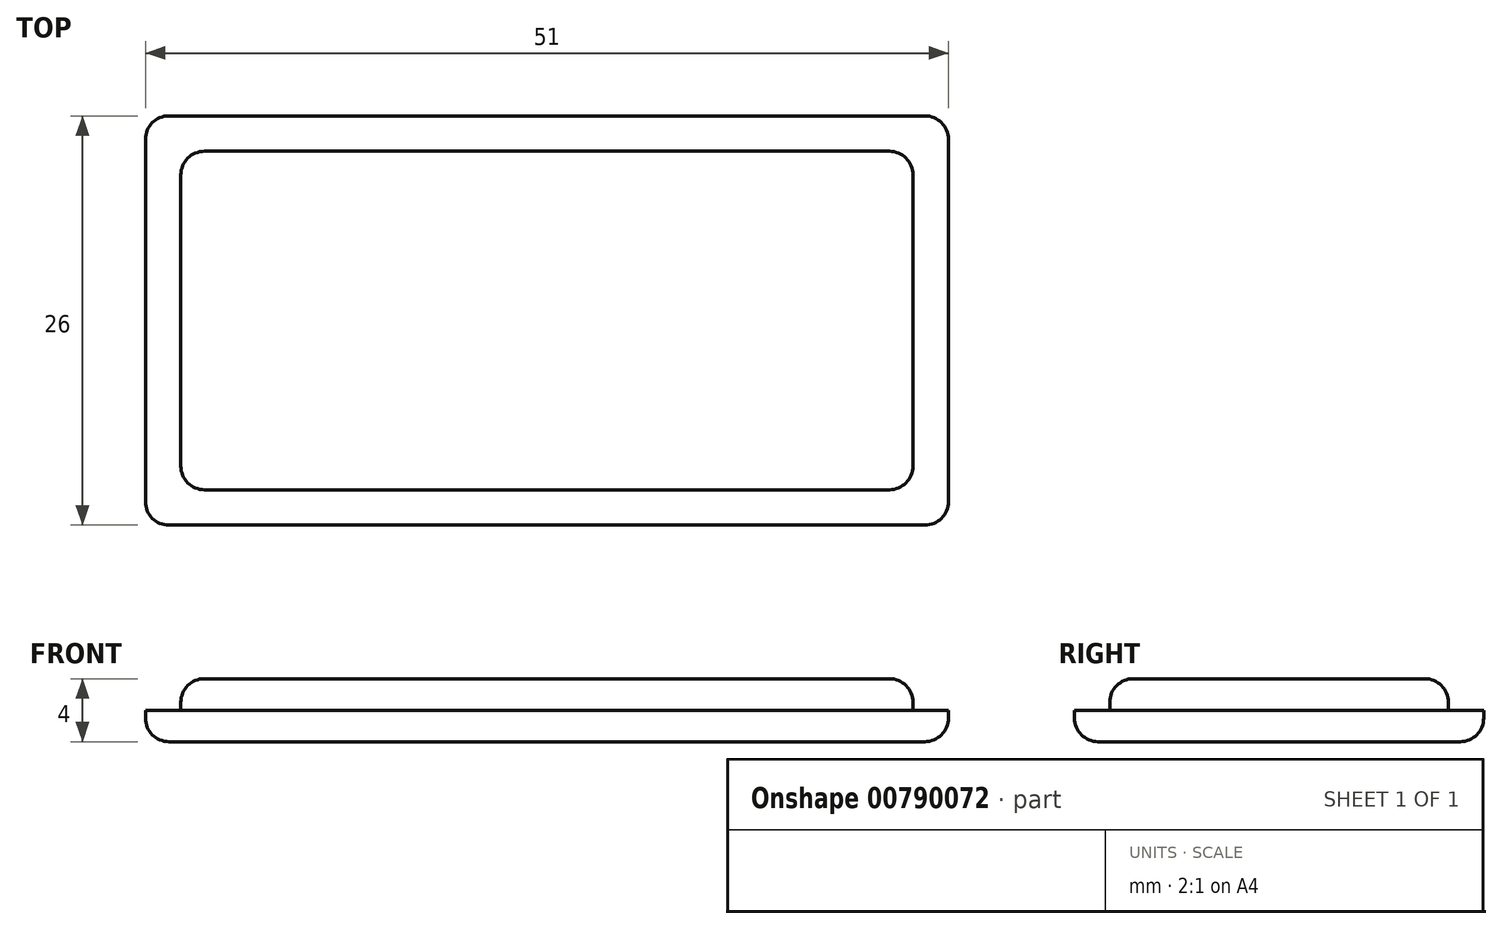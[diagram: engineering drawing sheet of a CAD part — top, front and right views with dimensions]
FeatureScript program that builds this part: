
annotation { "Feature Type Name" : "Feature", "Feature Type Description" : "" }
export const myFeature = defineFeature(function(context is Context, id is Id, definition is map)
    precondition{}
    {
        {
            var Q0;
            Q0=qCreatedBy(makeId("Top.planeOp"),FACE);
            var sketch = newSketch(context, id + "F0", { "sketchPlane" : qUnion([Q0])});
            skLineSegment(sketch, "E0.bottom", {"start": v(23.25, 10.75) * mm, "end": v(-23.25, 10.75) * mm});
            skLineSegment(sketch, "E0.top", {"start": v(23.25, -10.75) * mm, "end": v(-23.25, -10.75) * mm});
            skLineSegment(sketch, "E0.left", {"start": v(23.25, 10.75) * mm, "end": v(23.25, -10.75) * mm});
            skLineSegment(sketch, "E0.right", {"start": v(-23.25, 10.75) * mm, "end": v(-23.25, -10.75) * mm});
            skPoint(sketch, "E0.middle", {"position": v(0, 0) * mm});
            skLineSegment(sketch, "E1.bottom", {"start": v(25.5, 13) * mm, "end": v(-25.5, 13) * mm});
            skLineSegment(sketch, "E1.top", {"start": v(25.5, -13) * mm, "end": v(-25.5, -13) * mm});
            skLineSegment(sketch, "E1.left", {"start": v(25.5, 13) * mm, "end": v(25.5, -13) * mm});
            skLineSegment(sketch, "E1.right", {"start": v(-25.5, 13) * mm, "end": v(-25.5, -13) * mm});
            skSolve(sketch);
        }
        {
            var Q0;
            Q0 = qSketchRegion(id + "F0", true);
            extrude(context, id + "F1", {"entities" : qUnion([Q0]), "depth" : 2 * mm, "offsetDistance" : 25 * mm});
        }
        {
            var Q0;
            Q0=makeQuery(id+"F0.imprint","IMPRINT",FACE,{"disambiguationData":[TD([[makeQuery(id+"F0.imprint","IMPRINT",EDGE,{"derivedFrom":sQuery(id+"F0.wireOp",EDGE,"E0.bottom")}),1.0]])]});
            extrude(context, id + "F2", {"entities" : qUnion([Q0]), "operationType" : NewBodyOperationType.ADD, "depth" : 4 * mm, "offsetDistance" : 25 * mm});
        }
        {
            var Q0;
            Q0=makeQuery(id+"F1.opExtrude","SWEPT_EDGE",EDGE,{"disambiguationData":[OSD([sQuery(id+"F0.wireOp",EDGE,"E1.bottom"),sQuery(id+"F0.wireOp",EDGE,"E1.left")])]});
            var Q1;
            Q1=makeQuery(id+"F1.opExtrude","SWEPT_EDGE",EDGE,{"disambiguationData":[OSD([sQuery(id+"F0.wireOp",EDGE,"E1.bottom"),sQuery(id+"F0.wireOp",EDGE,"E1.right")])]});
            var Q2;
            Q2=makeQuery(id+"F1.opExtrude","SWEPT_EDGE",EDGE,{"disambiguationData":[OSD([sQuery(id+"F0.wireOp",EDGE,"E1.top"),sQuery(id+"F0.wireOp",EDGE,"E1.right")])]});
            var Q3;
            Q3=makeQuery(id+"F1.opExtrude","SWEPT_EDGE",EDGE,{"disambiguationData":[OSD([sQuery(id+"F0.wireOp",EDGE,"E1.top"),sQuery(id+"F0.wireOp",EDGE,"E1.left")])]});
            var Q4;
            Q4=makeQuery(id+"F1.opExtrude","CAP_EDGE",EDGE,{"disambiguationData":[OSD([sQuery(id+"F0.wireOp",EDGE,"E1.left")])],"isStart":true});
            var Q5;
            Q5=makeQuery(id+"F1.opExtrude","CAP_EDGE",EDGE,{"disambiguationData":[OSD([sQuery(id+"F0.wireOp",EDGE,"E1.top")])],"isStart":true});
            var Q6;
            Q6=makeQuery(id+"F1.opExtrude","CAP_EDGE",EDGE,{"disambiguationData":[OSD([sQuery(id+"F0.wireOp",EDGE,"E1.right")])],"isStart":true});
            var Q7;
            Q7=makeQuery(id+"F1.opExtrude","CAP_EDGE",EDGE,{"disambiguationData":[OSD([sQuery(id+"F0.wireOp",EDGE,"E1.bottom")])],"isStart":true});
            fillet(context, id + "F3", {"entities" : qUnion([Q0, Q1, Q2, Q3, Q4, Q5, Q6, Q7]), "radius" : 1.5 * mm, "tangentPropagation" : true, "allowEdgeOverflow" : false});
        }
        {
            var Q0;
            Q0=makeQuery(id+"F2.opExtrude","SWEPT_EDGE",EDGE,{"disambiguationData":[OSD([sQuery(id+"F0.wireOp",EDGE,"E0.top"),sQuery(id+"F0.wireOp",EDGE,"E0.right")])]});
            var Q1;
            Q1=makeQuery(id+"F2.opExtrude","SWEPT_EDGE",EDGE,{"disambiguationData":[OSD([sQuery(id+"F0.wireOp",EDGE,"E0.bottom"),sQuery(id+"F0.wireOp",EDGE,"E0.right")])]});
            var Q2;
            Q2=makeQuery(id+"F2.opExtrude","SWEPT_EDGE",EDGE,{"disambiguationData":[OSD([sQuery(id+"F0.wireOp",EDGE,"E0.bottom"),sQuery(id+"F0.wireOp",EDGE,"E0.left")])]});
            var Q3;
            Q3=makeQuery(id+"F2.opExtrude","SWEPT_EDGE",EDGE,{"disambiguationData":[OSD([sQuery(id+"F0.wireOp",EDGE,"E0.top"),sQuery(id+"F0.wireOp",EDGE,"E0.left")])]});
            var Q4;
            Q4=makeQuery(id+"F2.opExtrude","CAP_EDGE",EDGE,{"disambiguationData":[OSD([sQuery(id+"F0.wireOp",EDGE,"E0.left")])],"isStart":false});
            var Q5;
            Q5=makeQuery(id+"F2.opExtrude","CAP_EDGE",EDGE,{"disambiguationData":[OSD([sQuery(id+"F0.wireOp",EDGE,"E0.top")])],"isStart":false});
            var Q6;
            Q6=makeQuery(id+"F2.opExtrude","CAP_EDGE",EDGE,{"disambiguationData":[OSD([sQuery(id+"F0.wireOp",EDGE,"E0.right")])],"isStart":false});
            var Q7;
            Q7=makeQuery(id+"F2.opExtrude","CAP_EDGE",EDGE,{"disambiguationData":[OSD([sQuery(id+"F0.wireOp",EDGE,"E0.bottom")])],"isStart":false});
            fillet(context, id + "F4", {"entities" : qUnion([Q0, Q1, Q2, Q3, Q4, Q5, Q6, Q7]), "radius" : 1.5 * mm, "tangentPropagation" : true, "allowEdgeOverflow" : false});
        }
    });
